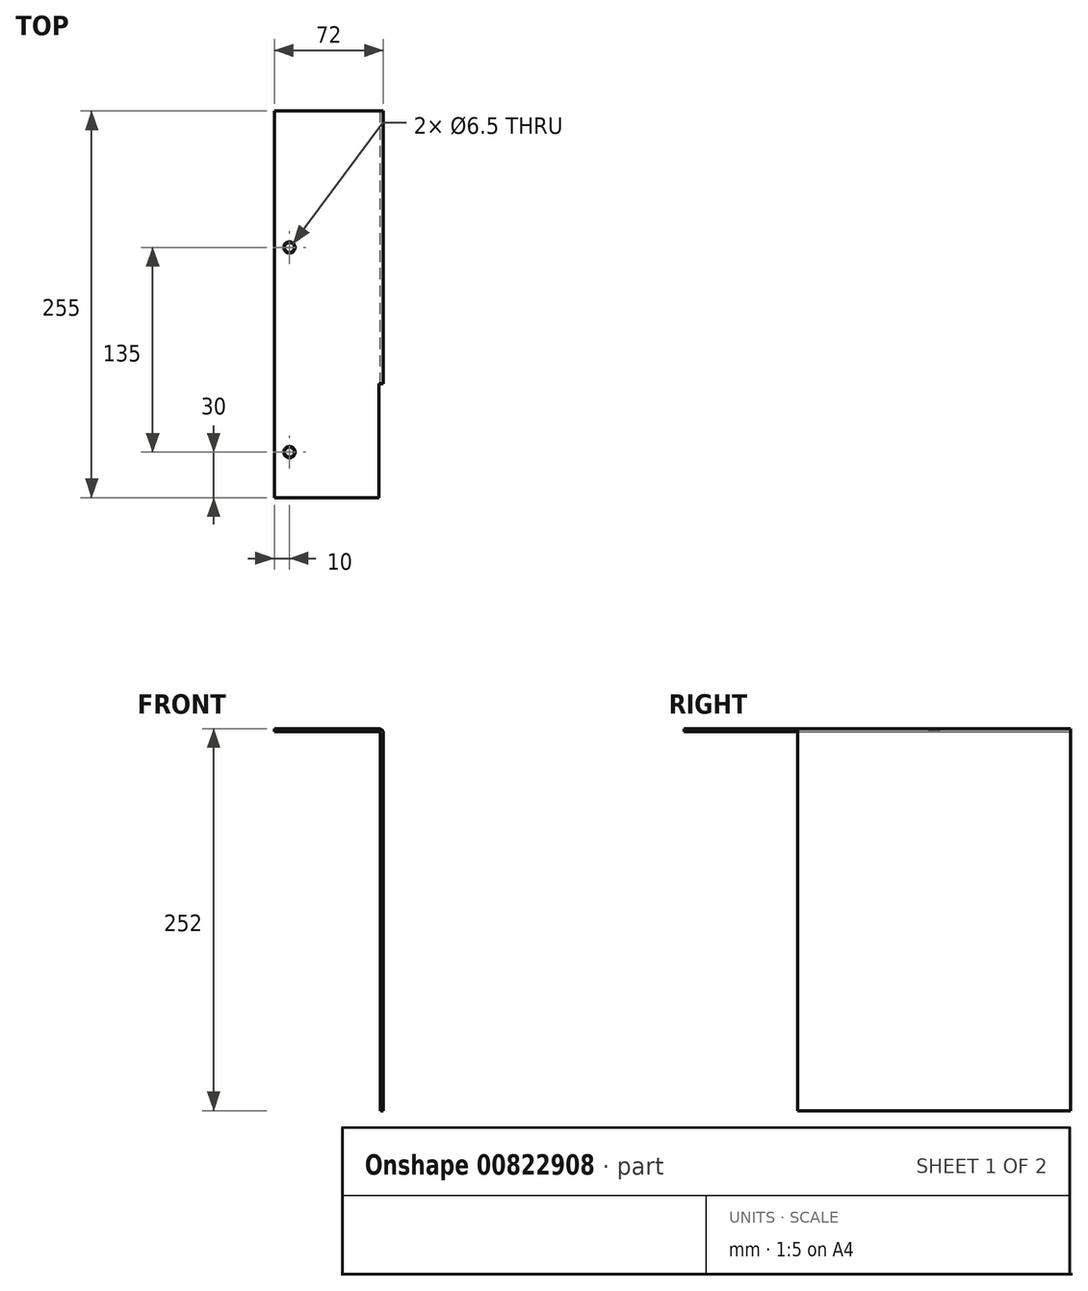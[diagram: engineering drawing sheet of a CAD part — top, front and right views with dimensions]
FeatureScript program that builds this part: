
annotation { "Feature Type Name" : "Feature", "Feature Type Description" : "" }
export const myFeature = defineFeature(function(context is Context, id is Id, definition is map)
    precondition{}
    {
        {
            var Q0;
            Q0=qCreatedBy(makeId("Front.planeOp"),FACE);
            var sketch = newSketch(context, id + "F0", { "sketchPlane" : qUnion([Q0])});
            skLineSegment(sketch, "E0", {"start": v(0, -1) * mm, "end": v(0, -250) * mm});
            skLineSegment(sketch, "E1", {"start": v(0, -250) * mm, "end": v(2, -250) * mm});
            skLineSegment(sketch, "E2", {"start": v(2, -250) * mm, "end": v(2, -1) * mm});
            skLineSegment(sketch, "E3", {"start": v(-1, 2) * mm, "end": v(-70, 2) * mm});
            skLineSegment(sketch, "E4", {"start": v(-70, 2) * mm, "end": v(-70, 0) * mm});
            skLineSegment(sketch, "E5", {"start": v(-70, 0) * mm, "end": v(-1, 0) * mm});
            skPoint(sketch, "E6.visualSharp", {"position": v(0, 0) * mm});
            skArc(sketch, "E6.filletArc", {"start": v(0, -1) * mm, "mid": v(-0.3, -0.3) * mm, "end": v(-1, 0) * mm});
            skPoint(sketch, "E7.visualSharp", {"position": v(2, 2) * mm});
            skArc(sketch, "E7.filletArc", {"start": v(2, -1) * mm, "mid": v(1.12, 1.12) * mm, "end": v(-1, 2) * mm});
            skSolve(sketch);
        }
        {
            var Q0;
            Q0 = qSketchRegion(id + "F0", true);
            extrude(context, id + "F1", {"entities" : qUnion([Q0]), "endBound" : BoundingType.SYMMETRIC, "depth" : 180 * mm, "offsetDistance" : 25 * mm});
        }
        {
            var Q0;
            Q0=makeQuery(id+"F1.opExtrude","CAP_FACE",FACE,{"disambiguationData":[OSD([sQuery(id+"F0.wireOp",EDGE,"E0"),sQuery(id+"F0.wireOp",EDGE,"E1"),sQuery(id+"F0.wireOp",EDGE,"E2"),sQuery(id+"F0.wireOp",EDGE,"E3"),sQuery(id+"F0.wireOp",EDGE,"E4"),sQuery(id+"F0.wireOp",EDGE,"E5"),sQuery(id+"F0.wireOp",EDGE,"E6.filletArc"),sQuery(id+"F0.wireOp",EDGE,"E7.filletArc")])],"isStart":false});
            var sketch = newSketch(context, id + "F2", { "sketchPlane" : qUnion([Q0])});
            skLineSegment(sketch, "E8.0", {"start": v(-1, 2) * mm, "end": v(-70, 2) * mm});
            skPoint(sketch, "E9.0", {"position": v(-70, 1) * mm});
            skLineSegment(sketch, "E10.0", {"start": v(-70, 0) * mm, "end": v(-1, 0) * mm});
            skLineSegment(sketch, "E11.0", {"start": v(-70, 2) * mm, "end": v(-70, 0) * mm});
            skLineSegment(sketch, "E12", {"start": v(-1, 0) * mm, "end": v(-1, 2) * mm});
            skSolve(sketch);
        }
        {
            var Q0;
            Q0 = qSketchRegion(id + "F2", true);
            extrude(context, id + "F3", {"entities" : qUnion([Q0]), "operationType" : NewBodyOperationType.ADD, "depth" : 75 * mm, "offsetDistance" : 25 * mm});
        }
        {
            var Q0;
            {var subQ0=sQuery(id+"F2.wireOp",EDGE,"E8.0");Q0=makeQuery(id+"FGcok9rtWQdlUR0_1.1.F3.boolean.opBoolean","MERGE",FACE,{"derivedFrom":[makeQuery(id+"F3.boolean.opBoolean","MERGE",FACE,{"derivedFrom":[makeQuery(id+"F1.opExtrude","SWEPT_FACE",FACE,{"disambiguationData":[OSD([sQuery(id+"F0.wireOp",EDGE,"E3")])]}),makeQuery(id+"F3.opExtrude","SWEPT_FACE",FACE,{"disambiguationData":[OSD([subQ0])]})]}),makeQuery(id+"FGcok9rtWQdlUR0_1.1.F3.opExtrude","SWEPT_FACE",FACE,{"disambiguationData":[OSD([subQ0])]})]});}
            var sketch = newSketch(context, id + "F4", { "sketchPlane" : qUnion([Q0])});
            skLineSegment(sketch, "E13.0.0", {"start": v(-1, -90) * mm, "end": v(-1, 90) * mm, "construction": true});
            skLineSegment(sketch, "E13.0.1", {"start": v(-1, 90) * mm, "end": v(-1, 165) * mm, "construction": true});
            skLineSegment(sketch, "E13.0.2", {"start": v(-1, 165) * mm, "end": v(-70, 165) * mm, "construction": true});
            skLineSegment(sketch, "E13.0.3", {"start": v(-70, 165) * mm, "end": v(-70, -165) * mm, "construction": true});
            skLineSegment(sketch, "E13.0.4", {"start": v(-70, -165) * mm, "end": v(-1, -165) * mm, "construction": true});
            skLineSegment(sketch, "E13.0.5", {"start": v(-1, -165) * mm, "end": v(-1, -90) * mm, "construction": true});
            skLineSegment(sketch, "E14", {"start": v(-60, 165) * mm, "end": v(-60, -165) * mm, "construction": true});
            skCircle(sketch, "E15", {"center": v(-60, 135) * mm, "radius": 3.25 * mm});
            skCircle(sketch, "E16.0.1.0", {"center": v(-60, 0) * mm, "radius": 3.25 * mm});
            skCircle(sketch, "E16.0.2.0", {"center": v(-60, -135) * mm, "radius": 3.25 * mm});
            skLineSegment(sketch, "E16.direction1", {"start": v(-60, 135) * mm, "end": v(85.02, 135) * mm, "construction": true});
            skLineSegment(sketch, "E16.direction2", {"start": v(-60, 135) * mm, "end": v(-60, 0) * mm, "construction": true});
            skSolve(sketch);
        }
        {
            var Q0;
            Q0 = qSketchRegion(id + "F4", true);
            extrude(context, id + "F5", {"entities" : qUnion([Q0]), "operationType" : NewBodyOperationType.REMOVE, "oppositeDirection" : true, "depth" : 25 * mm, "offsetDistance" : 25 * mm});
        }
        {
            var Q0;
            Q0=makeQuery(id+"F5.boolean.opBoolean","COPY",FACE,{"derivedFrom":makeQuery(id+"F5.opExtrude","SWEPT_FACE",FACE,{"disambiguationData":[OSD([sQuery(id+"F4.wireOp",EDGE,"E15")])]})});
            var Q1;
            Q1=makeQuery(id+"F5.boolean.opBoolean","COPY",FACE,{"derivedFrom":makeQuery(id+"F5.opExtrude","SWEPT_FACE",FACE,{"disambiguationData":[OSD([sQuery(id+"F4.wireOp",EDGE,"E16.0.1.0")])]})});
            var Q2;
            Q2=makeQuery(id+"F5.boolean.opBoolean","COPY",FACE,{"derivedFrom":makeQuery(id+"F5.opExtrude","SWEPT_FACE",FACE,{"disambiguationData":[OSD([sQuery(id+"F4.wireOp",EDGE,"E16.0.2.0")])]})});
            chamfer(context, id + "F6", {"entities" : qUnion([Q0, Q1, Q2]), "width" : 0.5 * mm, "tangentPropagation" : true});
        }
    });
